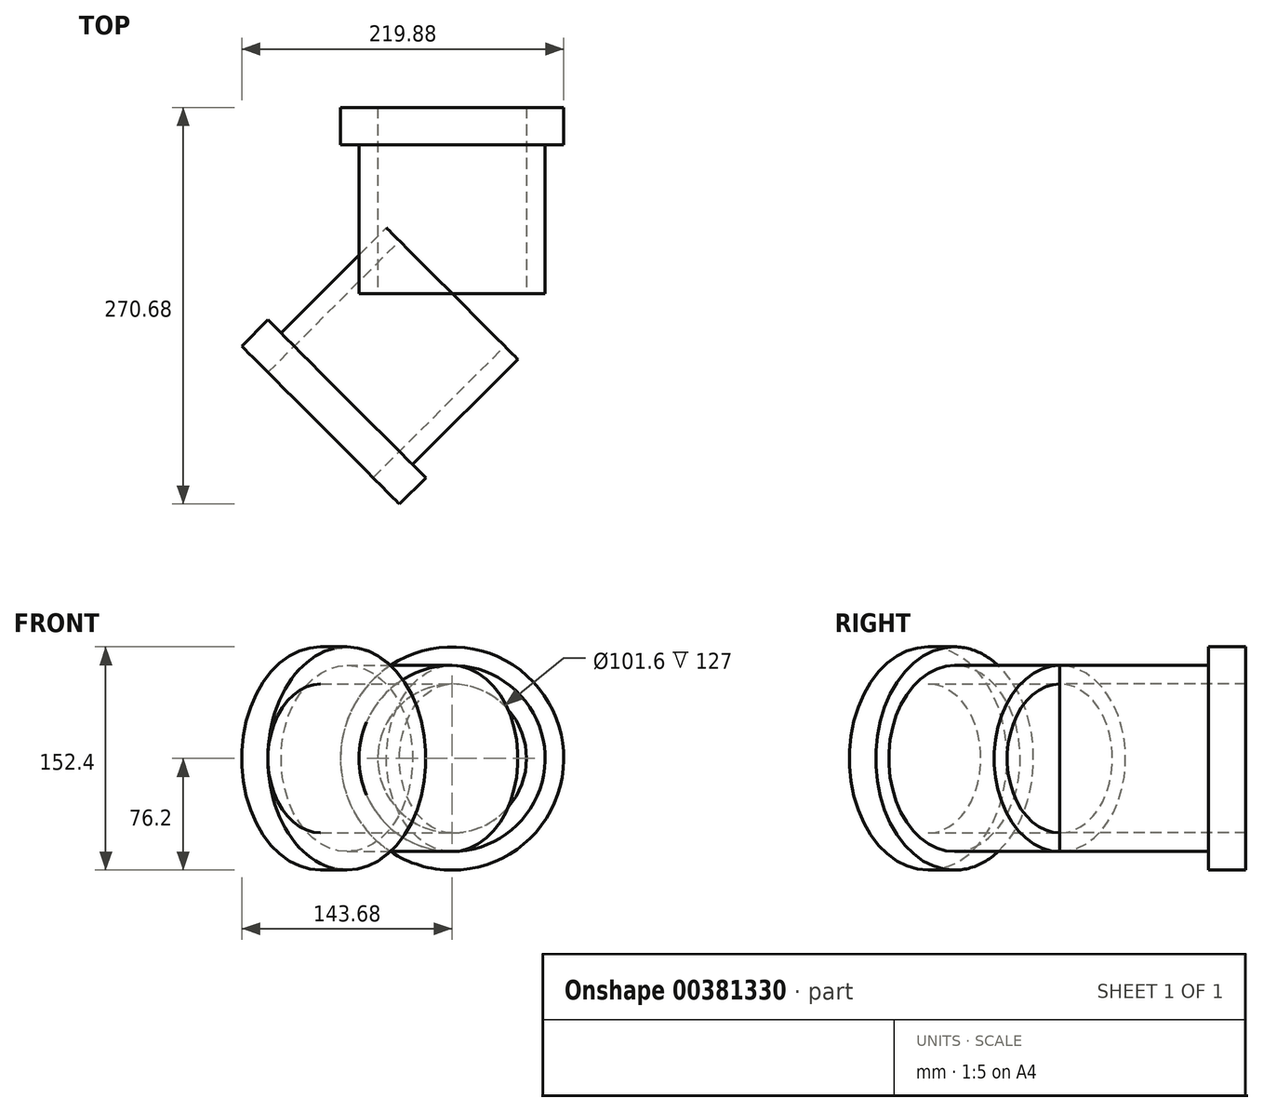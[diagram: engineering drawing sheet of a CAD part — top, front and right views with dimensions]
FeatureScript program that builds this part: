
annotation { "Feature Type Name" : "Feature", "Feature Type Description" : "" }
export const myFeature = defineFeature(function(context is Context, id is Id, definition is map)
    precondition{}
    {
        {
            var Q0;
            Q0=qCreatedBy(makeId("Top.planeOp"),FACE);
            var sketch = newSketch(context, id + "F0", { "sketchPlane" : qUnion([Q0])});
            skLineSegment(sketch, "E0", {"start": v(50.8, 0) * mm, "end": v(50.8, 127) * mm});
            skLineSegment(sketch, "E1", {"start": v(50.8, 127) * mm, "end": v(76.2, 127) * mm});
            skLineSegment(sketch, "E2", {"start": v(76.2, 127) * mm, "end": v(76.2, 101.6) * mm});
            skLineSegment(sketch, "E3", {"start": v(76.2, 101.6) * mm, "end": v(63.5, 101.6) * mm});
            skLineSegment(sketch, "E4", {"start": v(63.5, 101.6) * mm, "end": v(63.5, 0) * mm});
            skLineSegment(sketch, "E5", {"start": v(63.5, 0) * mm, "end": v(50.8, 0) * mm});
            skSolve(sketch);
        }
        {
            var Q0;
            Q0=qCreatedBy(makeId("Right.planeOp"),FACE);
            var sketch = newSketch(context, id + "F1", { "sketchPlane" : qUnion([Q0])});
            skLineSegment(sketch, "E6", {"start": v(0, 0) * mm, "end": v(198.44, 0) * mm});
            skSolve(sketch);
        }
        {
            var Q0;
            Q0=makeQuery(id+"F0.imprint","IMPRINT",FACE,{"disambiguationData":[TD([[makeQuery(id+"F0.imprint","IMPRINT",EDGE,{"derivedFrom":sQuery(id+"F0.wireOp",EDGE,"E0")}),-1.0]])]});
            var Q1;
            Q1=sQuery(id+"F1.wireOp",EDGE,"E6");
            revolve(context, id + "F2", {"entities" : qUnion([Q0]), "axis" : qUnion([Q1]), "revolveType" : RevolveType.ONE_DIRECTION, "angle" : 360 * degree});
        }
        {
            var Q0;
            Q0=qCreatedBy(makeId("Front.planeOp"),FACE);
            var sketch = newSketch(context, id + "F3", { "sketchPlane" : qUnion([Q0])});
            skLineSegment(sketch, "E7", {"start": v(0, 0) * mm, "end": v(0, 184.78) * mm});
            skSolve(sketch);
        }
        {
            var Q0;
            Q0=makeQuery(id+"F2.opRevolve","SWEPT_BODY",BODY,{"disambiguationData":[OSD([sQuery(id+"F0.wireOp",EDGE,"E0"),sQuery(id+"F0.wireOp",EDGE,"E1"),sQuery(id+"F0.wireOp",EDGE,"E2"),sQuery(id+"F0.wireOp",EDGE,"E3"),sQuery(id+"F0.wireOp",EDGE,"E4"),sQuery(id+"F0.wireOp",EDGE,"E5")])]});
            var Q1;
            Q1=sQuery(id+"F3.wireOp",EDGE,"E7");
            transform(context, id + "F4", {"entities" : qUnion([Q0]), "transformType" : TransformType.ROTATION, "transformAxis" : qUnion([Q1]), "angle" : 135 * degree, "makeCopy" : true});
        }
    });
